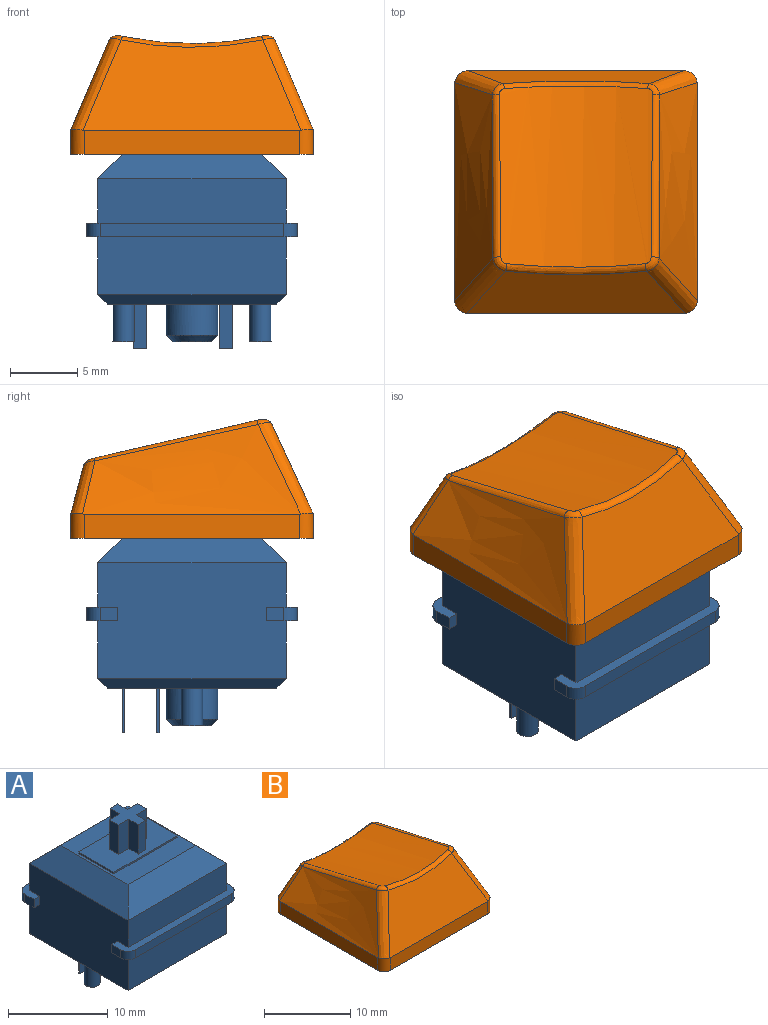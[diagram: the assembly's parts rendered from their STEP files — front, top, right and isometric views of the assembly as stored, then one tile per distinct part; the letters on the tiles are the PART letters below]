
ASSEMBLY  parts=2 mates=1
PART A: 69 faces, bbox 15.6x15.6x18.6 mm
  f0: plane 15.6x2.3mm, normal (0,0,-1), area 14.4mm2, adj f2,f3,f28,f30,f35,f60,f62,f63
  f1: plane 15.6x2.3mm, normal (0,0,-1), area 14.4mm2, adj f28,f30,f33,f34,f36,f59,f61,f64
  f2: plane 1.3x1mm, normal (1,0,0), area 1.3mm2, adj f0,f32,f62,f66
  f3: plane 1.3x1mm, normal (-1,0,0), area 1.3mm2, adj f0,f32,f63,f68
  f4: plane 15.6x2.3mm, normal (0,0,1), area 14.4mm2, adj f28,f30,f31,f33,f34,f36,f61,f64
  f5: plane 14x2.2mm, normal (-0.71,0,0.71), area 36.7mm2, adj f6,f7,f26,f30
  f6: plane 14x2.2mm, normal (0,-0.71,0.71), area 36.7mm2, adj f5,f7,f27,f31
  f7: plane 9.6x9.6mm, normal (0,0,1), area 47.2mm2, adj f5,f6,f8,f9,f10,f11,f26,f27
  f8: plane 5x0.2mm, normal (1,0,0), area 1mm2, adj f7,f9,f11,f12
  f9: plane 9x0.2mm, normal (0,1,0), area 1.8mm2, adj f7,f8,f10,f12
  f10: plane 5x0.2mm, normal (-1,0,0), area 1mm2, adj f7,f9,f11,f12
  f11: plane 9x0.2mm, normal (0,-1,0), area 1.8mm2, adj f7,f8,f10,f12
  f12: plane 9x5mm, normal (0,0,1), area 36.9mm2, adj f8,f9,f10,f11,f13,f14,f15,f16
  f13: plane 3.6x1.35mm, normal (1,0,0), area 4.9mm2, adj f12,f14,f24,f25
  f14: plane 3.6x1.08mm, normal (0,1,0), area 3.9mm2, adj f12,f13,f15,f25
  f15: plane 3.6x1.35mm, normal (-1,0,0), area 4.9mm2, adj f12,f14,f16,f25
  f16: plane 3.6x1.46mm, normal (0,1,0), area 5.3mm2, adj f12,f15,f17,f25
  f17: plane 3.6x1.3mm, normal (-1,0,0), area 4.7mm2, adj f12,f16,f18,f25
  f18: plane 3.6x1.46mm, normal (0,-1,0), area 5.3mm2, adj f12,f17,f19,f25
  f19: plane 3.6x1.35mm, normal (-1,0,0), area 4.9mm2, adj f12,f18,f20,f25
  f20: plane 3.6x1.08mm, normal (0,-1,0), area 3.9mm2, adj f12,f19,f21,f25
  f21: plane 3.6x1.35mm, normal (1,0,0), area 4.9mm2, adj f12,f20,f22,f25
  f22: plane 3.6x1.46mm, normal (0,-1,0), area 5.3mm2, adj f12,f21,f23,f25
  f23: plane 3.6x1.3mm, normal (1,0,0), area 4.7mm2, adj f12,f22,f24,f25
  f24: plane 3.6x1.46mm, normal (0,1,0), area 5.3mm2, adj f12,f13,f23,f25
  f25: plane 4x4mm, normal (0,0,1), area 8.1mm2, adj f13,f14,f15,f16,f17,f18,f19,f20
  f26: plane 14x2.2mm, normal (0,0.71,0.71), area 36.7mm2, adj f5,f7,f27,f29
  f27: plane 14x2.2mm, normal (0.71,0,0.71), area 36.7mm2, adj f6,f7,f26,f28
  f28: plane 14x8.6mm, normal (1,0,0), area 117.4mm2, adj f0,f1,f4,f27,f29,f31,f32,f55
  f29: plane 14x3.3mm, normal (0,1,0), area 46.2mm2, adj f26,f28,f30,f32
  f30: plane 14x8.6mm, normal (-1,0,0), area 117.4mm2, adj f0,f1,f4,f5,f29,f31,f32,f57
  f31: plane 14x3.3mm, normal (0,-1,0), area 46.2mm2, adj f4,f6,f28,f30
  f32: plane 15.6x2.3mm, normal (0,0,1), area 14.4mm2, adj f2,f3,f28,f29,f30,f35,f62,f63
  f33: plane 13.6x1mm, normal (0,-1,0), area 13.6mm2, adj f1,f4,f61,f64
  f34: plane 1.3x1mm, normal (1,0,0), area 1.3mm2, adj f1,f4,f61,f65
  f35: plane 13.6x1mm, normal (0,1,0), area 13.6mm2, adj f0,f32,f62,f63
  f36: plane 1.3x1mm, normal (-1,0,0), area 1.3mm2, adj f1,f4,f64,f67
  f37: plane 2.85x2.85mm, normal (0,0,-1), area 6.4mm2, adj f38
  f38: cone r=1.43mm half-angle=45deg, axis (0,0,1), area 7.4mm2, adj f37,f43
  f39: plane 1x0.2mm, normal (0,0,-1), area 0.2mm2, adj f44,f45,f46,f47
  f40: plane 1x0.2mm, normal (0,0,-1), area 0.2mm2, adj f48,f49,f50,f51
  f41: plane 1.6x1.6mm, normal (0,0,-1), area 2mm2, adj f52
  f42: plane 1.6x1.6mm, normal (0,0,-1), area 2mm2, adj f53
  f43: cylinder r=1.93mm len=3.85mm, axis (0,0,1), area 27.8mm2, adj f38,f54
  f44: plane 3.3x0.2mm, normal (-1,0,0), area 0.7mm2, adj f39,f45,f47,f54
  f45: plane 3.3x1mm, normal (0,1,0), area 3.3mm2, adj f39,f44,f46,f54
  f46: plane 3.3x0.2mm, normal (1,0,0), area 0.7mm2, adj f39,f45,f47,f54
  f47: plane 3.3x1mm, normal (0,-1,0), area 3.3mm2, adj f39,f44,f46,f54
  f48: plane 3.3x0.2mm, normal (-1,0,0), area 0.7mm2, adj f40,f49,f51,f54
  f49: plane 3.3x1mm, normal (0,1,0), area 3.3mm2, adj f40,f48,f50,f54
  f50: plane 3.3x0.2mm, normal (1,0,0), area 0.7mm2, adj f40,f49,f51,f54
  f51: plane 3.3x1mm, normal (0,-1,0), area 3.3mm2, adj f40,f48,f50,f54
  f52: cylinder r=0.8mm len=2.8mm, axis (0,0,1), area 14.1mm2, adj f41,f54
  f53: cylinder r=0.8mm len=2.8mm, axis (0,0,1), area 14.1mm2, adj f42,f54
  f54: plane 12.6x12.6mm, normal (0,0,-1), area 142.7mm2, adj f43,f44,f45,f46,f47,f48,f49,f50
  f55: plane 14x0.7mm, normal (0.71,0,-0.71), area 13.2mm2, adj f28,f54,f56,f58
  f56: plane 14x0.7mm, normal (0,0.71,-0.71), area 13.2mm2, adj f54,f55,f57,f60
  f57: plane 14x0.7mm, normal (-0.71,0,-0.71), area 13.2mm2, adj f30,f54,f56,f58
  f58: plane 14x0.7mm, normal (0,-0.71,-0.71), area 13.2mm2, adj f54,f55,f57,f59
  f59: plane 14x4.3mm, normal (0,-1,0), area 60.2mm2, adj f1,f28,f30,f58
  f60: plane 14x4.3mm, normal (0,1,0), area 60.2mm2, adj f0,f28,f30,f56
  f61: cylinder r=1mm len=1mm, axis (0,0,-1), area 1.6mm2, adj f1,f4,f33,f34
  f62: cylinder r=1mm len=1mm, axis (0,0,1), area 1.6mm2, adj f0,f2,f32,f35
  f63: cylinder r=1mm len=1mm, axis (0,0,-1), area 1.6mm2, adj f0,f3,f32,f35
  f64: cylinder r=1mm len=1mm, axis (0,0,1), area 1.6mm2, adj f1,f4,f33,f36
  f65: plane 1x0.8mm, normal (0,1,0), area 0.8mm2, adj f1,f4,f28,f34
  f66: plane 1x0.8mm, normal (0,-1,0), area 0.8mm2, adj f0,f2,f28,f32
  f67: plane 1x0.8mm, normal (0,1,0), area 0.8mm2, adj f1,f4,f30,f36
  f68: plane 1x0.8mm, normal (0,-1,0), area 0.8mm2, adj f0,f3,f30,f32
PART B: 50 faces, bbox 21.5x21.7x12.5 mm
  f0: plane 18x18mm, normal (0,0,-1), area 67.1mm2, adj f1,f2,f3,f4,f10,f12,f14,f16
  f1: plane 16x1.8mm, normal (1,0,0), area 28.8mm2, adj f0,f8,f10,f16
  f2: plane 16x1.8mm, normal (0,1,0), area 28.8mm2, adj f0,f5,f14,f15,f16,f17
  f3: plane 16x1.8mm, normal (-1,0,0), area 28.8mm2, adj f0,f6,f12,f14
  f4: plane 16x1.8mm, normal (0,-1,0), area 28.8mm2, adj f0,f7,f10,f12
  f5: plane 15.91x3.6mm, normal (0,0.97,0.26), area 44.6mm2, adj f2,f15,f17,f20
  f6: bspline ~18x7.25mm, area 86.5mm2, adj f3,f12,f13,f14,f15,f19
  f7: plane 16.18x6.7mm, normal (0,-0.91,0.42), area 94.1mm2, adj f4,f10,f11,f12,f13,f23
  f8: bspline ~18x7.25mm, area 86.5mm2, adj f1,f10,f11,f16,f17,f24
  f9: cylinder r=22.9mm len=13.49mm, axis (0,0.97,-0.23), area 153.8mm2, adj f18,f19,f20,f21,f22,f23,f24,f25
  f10: cylinder r=1mm len=1.88mm, axis (0,0,-1), area 2.9mm2, adj f0,f1,f4,f7,f8,f11
  f11: bspline ~9.03x5.02mm, area 11.4mm2, adj f7,f8,f10,f25
  f12: cylinder r=1mm len=1.88mm, axis (0,0,1), area 2.9mm2, adj f0,f3,f4,f6,f7,f13
  f13: bspline ~10.12x5.54mm, area 11.4mm2, adj f6,f7,f12,f21
  f14: cylinder r=1mm len=1.81mm, axis (0,0,-1), area 2.8mm2, adj f0,f2,f3,f6,f15
  f15: bspline ~6.35x5.01mm, area 6.5mm2, adj f2,f5,f6,f14,f18
  f16: cylinder r=1mm len=1.81mm, axis (0,0,1), area 2.8mm2, adj f0,f1,f2,f8,f17
  f17: bspline ~6.25x4.94mm, area 6.5mm2, adj f2,f5,f8,f16,f22
  f18: bspline ~1.11x0.93mm, area 0.5mm2, adj f9,f15,f19,f20
  f19: bspline ~17.83x4.37mm, area 8.2mm2, adj f6,f9,f18,f21
  f20: bspline ~10.85x1.04mm, area 5.9mm2, adj f5,f9,f18,f22
  f21: bspline ~1.22x1.15mm, area 0.8mm2, adj f9,f13,f19,f23
  f22: bspline ~1.11x1.06mm, area 0.5mm2, adj f9,f17,f20,f24
  f23: bspline ~10.49x0.83mm, area 7.2mm2, adj f7,f9,f21,f25
  f24: bspline ~17.79x4.36mm, area 8.2mm2, adj f8,f9,f22,f25
  f25: bspline ~1.31x1.07mm, area 0.8mm2, adj f9,f11,f23,f24
  f26: plane 16.1x1.69mm, normal (-1,0,0), area 24.8mm2, adj f0,f27,f29,f33
  f27: plane 16x1.67mm, normal (0,-1,0), area 26.7mm2, adj f0,f26,f28,f30,f31,f33
  f28: plane 16.1x1.69mm, normal (1,0,0), area 24.8mm2, adj f0,f27,f29,f31
  f29: plane 16x1.59mm, normal (0,1,0), area 25.3mm2, adj f0,f26,f28,f32
  f30: plane 16.45x3.93mm, normal (0,-0.97,-0.26), area 39.2mm2, adj f27,f31,f33,f34
  f31: offset ~20x9.25mm, area 77.4mm2, adj f27,f28,f30,f32,f34
  f32: plane 16.26x6.4mm, normal (0,0.91,-0.42), area 86.2mm2, adj f29,f31,f33,f34
  f33: offset ~20x9.25mm, area 77.3mm2, adj f26,f27,f30,f32,f34
  f34: cylinder r=23.9mm len=12.44mm, axis (0,0.97,-0.23), area 115.6mm2, adj f30,f31,f32,f33,f46
  f35: plane 5.13x1.5mm, normal (-1,0,0), area 7.4mm2, adj f36,f44,f45,f49
  f36: plane 5.23x1.51mm, normal (0,-1,0), area 7.8mm2, adj f35,f37,f45,f49
  f37: plane 5.53x1.3mm, normal (-1,0,0), area 7mm2, adj f36,f38,f45,f49
  f38: plane 5.53x1.51mm, normal (0,1,0), area 8.2mm2, adj f37,f39,f45,f49
  f39: plane 5.79x1.5mm, normal (-1,0,0), area 8.4mm2, adj f38,f40,f45,f49
  f40: plane 5.79x1.3mm, normal (0,1,0), area 7.5mm2, adj f39,f41,f45,f49
  f41: plane 5.79x1.5mm, normal (1,0,0), area 8.4mm2, adj f40,f42,f45,f49
  f42: plane 5.53x1.51mm, normal (0,1,0), area 8.2mm2, adj f41,f43,f45,f49
  f43: plane 5.53x1.3mm, normal (1,0,0), area 7mm2, adj f42,f45,f47,f49
  f44: plane 4.79x1.3mm, normal (0,-1,0), area 6.2mm2, adj f35,f45,f48,f49
  f45: plane 5.5x5.5mm, normal (0,0,-1), area 14.3mm2, adj f35,f36,f37,f38,f39,f40,f41,f42
  f46: cylinder r=2.75mm len=5.5mm, axis (0,0,-1), area 94mm2, adj f34,f45
  f47: plane 5.23x1.51mm, normal (0,-1,0), area 7.8mm2, adj f43,f45,f48,f49
  f48: plane 5.13x1.5mm, normal (1,0,0), area 7.4mm2, adj f44,f45,f47,f49
  f49: cylinder r=23.9mm len=4.32mm, axis (0,0.97,-0.23), area 9.8mm2, adj f35,f36,f37,f38,f39,f40,f41,f42
PLACE A at identity fixed
PLACE B t=(0,0,11.1)mm
MATE fastened A.f38 <-> B.f46  axis (0,0,1) through (0,0,11.7)mm
